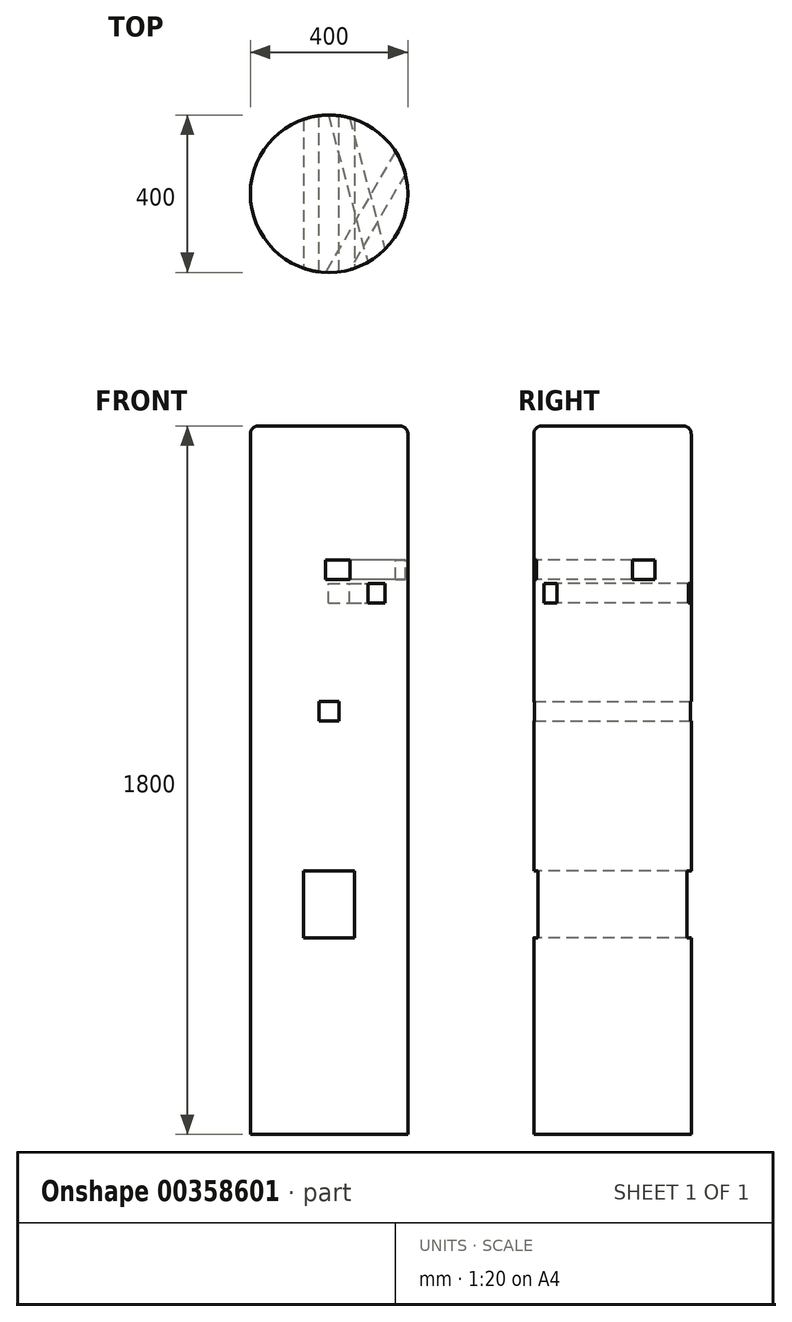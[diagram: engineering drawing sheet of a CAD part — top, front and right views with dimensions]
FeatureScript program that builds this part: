
annotation { "Feature Type Name" : "Feature", "Feature Type Description" : "" }
export const myFeature = defineFeature(function(context is Context, id is Id, definition is map)
    precondition{}
    {
        {
            var Q0;
            Q0=qCreatedBy(makeId("Top.planeOp"),FACE);
            var sketch = newSketch(context, id + "F0", { "sketchPlane" : qUnion([Q0])});
            skCircle(sketch, "E0", {"center": v(0, 0) * mm, "radius": 200 * mm});
            skSolve(sketch);
        }
        {
            var Q0;
            Q0 = qSketchRegion(id + "F0", true);
            extrude(context, id + "F1", {"entities" : qUnion([Q0]), "oppositeDirection" : true, "depth" : 1800 * mm});
        }
        {
            var Q0;
            Q0=qCreatedBy(makeId("Front.planeOp"),FACE);
            var sketch = newSketch(context, id + "F2", { "sketchPlane" : qUnion([Q0])});
            skLineSegment(sketch, "E1.bottom", {"start": v(65, -1300) * mm, "end": v(-65, -1300) * mm});
            skLineSegment(sketch, "E1.top", {"start": v(65, -1130) * mm, "end": v(-65, -1130) * mm});
            skLineSegment(sketch, "E1.left", {"start": v(65, -1300) * mm, "end": v(65, -1130) * mm});
            skLineSegment(sketch, "E1.right", {"start": v(-65, -1300) * mm, "end": v(-65, -1130) * mm});
            skPoint(sketch, "E1.middle", {"position": v(0, -1215) * mm});
            skSolve(sketch);
        }
        {
            var Q0;
            Q0 = qSketchRegion(id + "F2", true);
            extrude(context, id + "F3", {"entities" : qUnion([Q0]), "operationType" : NewBodyOperationType.REMOVE, "endBound" : BoundingType.SYMMETRIC, "oppositeDirection" : true, "depth" : 1000 * mm});
        }
        {
            var Q0;
            Q0=qCreatedBy(makeId("Front.planeOp"),FACE);
            var sketch = newSketch(context, id + "F4", { "sketchPlane" : qUnion([Q0])});
            skLineSegment(sketch, "E2.bottom", {"start": v(25, -750) * mm, "end": v(-25, -750) * mm});
            skLineSegment(sketch, "E2.top", {"start": v(25, -700) * mm, "end": v(-25, -700) * mm});
            skLineSegment(sketch, "E2.left", {"start": v(25, -750) * mm, "end": v(25, -700) * mm});
            skLineSegment(sketch, "E2.right", {"start": v(-25, -750) * mm, "end": v(-25, -700) * mm});
            skPoint(sketch, "E2.middle", {"position": v(0, -725) * mm});
            skSolve(sketch);
        }
        {
            var Q0;
            Q0 = qSketchRegion(id + "F4", true);
            extrude(context, id + "F5", {"entities" : qUnion([Q0]), "operationType" : NewBodyOperationType.REMOVE, "endBound" : BoundingType.SYMMETRIC, "depth" : 1000 * mm});
        }
        {
            var Q0;
            Q0=qCreatedBy(makeId("Front.planeOp"),FACE);
            var sketch = newSketch(context, id + "F6", { "sketchPlane" : qUnion([Q0])});
            skLineSegment(sketch, "E3", {"start": v(0, 0) * mm, "end": v(0, -1840.16) * mm});
            skSolve(sketch);
        }
        {
            var Q0;
            Q0=sQuery(id+"F6.wireOp",EDGE,"E3");
            var Q1;
            Q1=qCreatedBy(makeId("Front.planeOp"),FACE);
            cPlane(context, id + "F7", {"entities" : qUnion([Q0, Q1]), "cplaneType" : CPlaneType.LINE_ANGLE, "offset" : 25 * mm, "angle" : 15 * degree, "oppositeDirection" : true, "width" : 150 * mm, "height" : 150 * mm});
        }
        {
            var Q0;
            Q0=qCreatedBy(id+"F7.planeOp",FACE);
            var sketch = newSketch(context, id + "F8", { "sketchPlane" : qUnion([Q0])});
            skLineSegment(sketch, "E4.bottom", {"start": v(-50, -450) * mm, "end": v(-100, -450) * mm});
            skLineSegment(sketch, "E4.top", {"start": v(-50, -400) * mm, "end": v(-100, -400) * mm});
            skLineSegment(sketch, "E4.left", {"start": v(-50, -450) * mm, "end": v(-50, -400) * mm});
            skLineSegment(sketch, "E4.right", {"start": v(-100, -450) * mm, "end": v(-100, -400) * mm});
            skPoint(sketch, "E4.middle", {"position": v(-75, -425) * mm});
            skSolve(sketch);
        }
        {
            var Q0;
            Q0 = qSketchRegion(id + "F8", true);
            extrude(context, id + "F9", {"entities" : qUnion([Q0]), "operationType" : NewBodyOperationType.REMOVE, "endBound" : BoundingType.SYMMETRIC, "depth" : 1000 * mm});
        }
        {
            var Q0;
            Q0=sQuery(id+"F6.wireOp",EDGE,"E3");
            var Q1;
            Q1=qCreatedBy(makeId("Front.planeOp"),FACE);
            cPlane(context, id + "F10", {"entities" : qUnion([Q0, Q1]), "cplaneType" : CPlaneType.LINE_ANGLE, "offset" : 25 * mm, "angle" : 30 * degree, "width" : 150 * mm, "height" : 150 * mm});
        }
        {
            var Q0;
            Q0=qCreatedBy(id+"F10.planeOp",FACE);
            var sketch = newSketch(context, id + "F11", { "sketchPlane" : qUnion([Q0])});
            skLineSegment(sketch, "E5.bottom", {"start": v(-92.29, -390) * mm, "end": v(-142.29, -390) * mm});
            skLineSegment(sketch, "E5.top", {"start": v(-92.29, -340) * mm, "end": v(-142.29, -340) * mm});
            skLineSegment(sketch, "E5.left", {"start": v(-92.29, -390) * mm, "end": v(-92.29, -340) * mm});
            skLineSegment(sketch, "E5.right", {"start": v(-142.29, -390) * mm, "end": v(-142.29, -340) * mm});
            skPoint(sketch, "E5.middle", {"position": v(-117.29, -365) * mm});
            skSolve(sketch);
        }
        {
            var Q0;
            Q0 = qSketchRegion(id + "F11", true);
            extrude(context, id + "F12", {"entities" : qUnion([Q0]), "operationType" : NewBodyOperationType.REMOVE, "endBound" : BoundingType.SYMMETRIC, "depth" : 1000 * mm});
        }
        {
            var Q0;
            Q0=makeQuery(id+"F1.opExtrude","CAP_EDGE",EDGE,{"disambiguationData":[OSD([sQuery(id+"F0.wireOp",EDGE,"E0")])],"isStart":true});
            fillet(context, id + "F13", {"entities" : qUnion([Q0]), "radius" : 20 * mm, "tangentPropagation" : true, "allowEdgeOverflow" : false});
        }
    });
